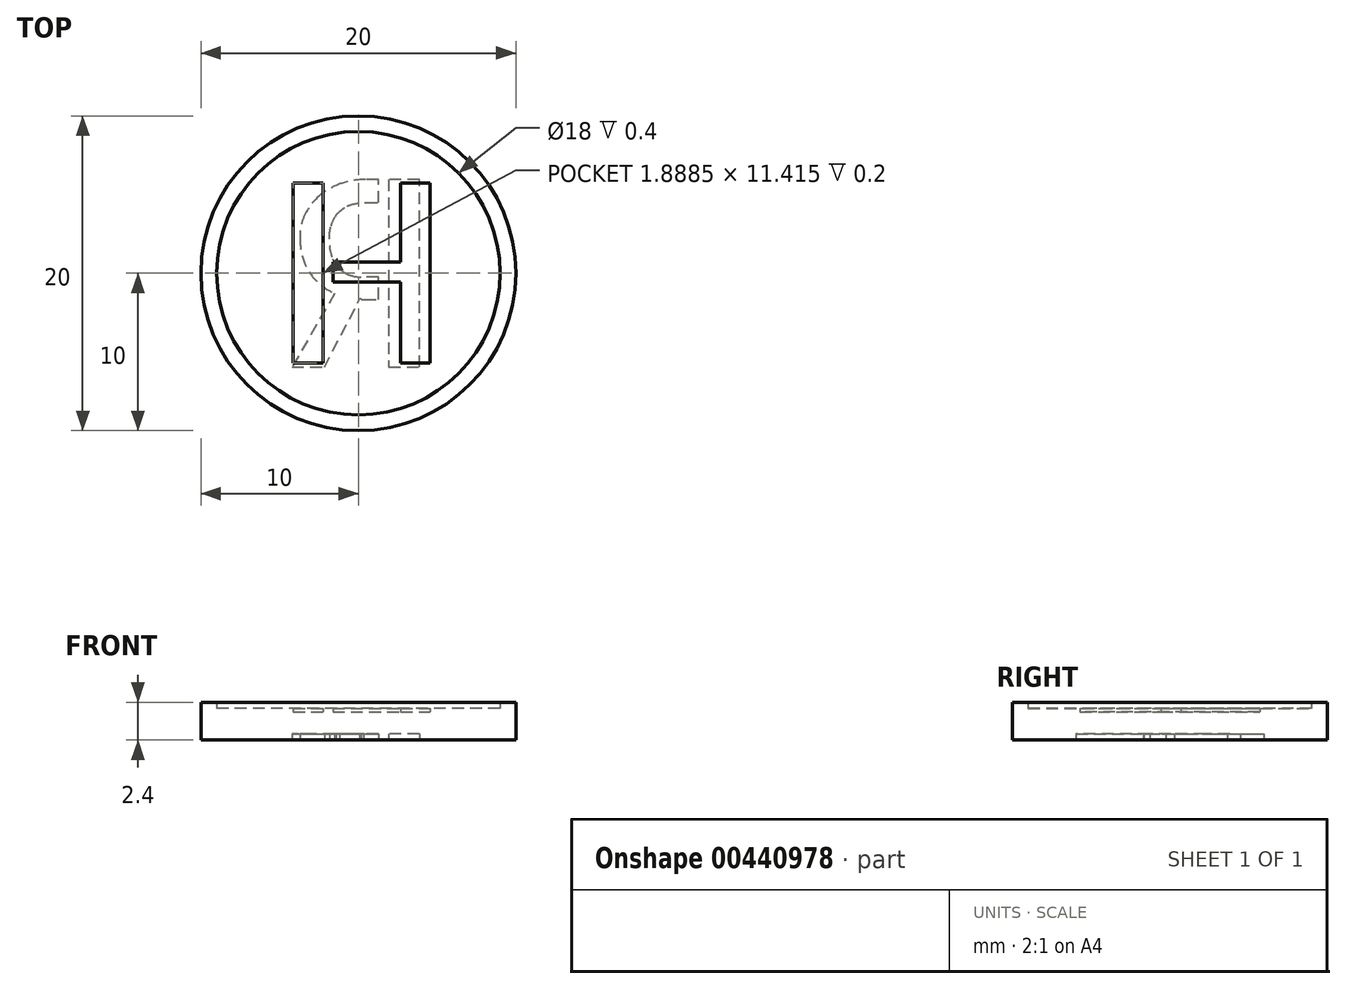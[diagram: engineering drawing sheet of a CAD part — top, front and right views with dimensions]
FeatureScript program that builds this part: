
annotation { "Feature Type Name" : "Feature", "Feature Type Description" : "" }
export const myFeature = defineFeature(function(context is Context, id is Id, definition is map)
    precondition{}
    {
        {
            var Q0;
            Q0=qCreatedBy(makeId("Top.planeOp"),FACE);
            var sketch = newSketch(context, id + "F0", { "sketchPlane" : qUnion([Q0])});
            skCircle(sketch, "E0", {"center": v(0, 0) * mm, "radius": 10 * mm});
            skText(sketch, "E1", { "text": "H", "fontName": "AllertaStencil-Regular.ttf"});
            const initialGuessF0  = {"E1": [-0.0056, -0.0057, 1, 0, 0.01142]};
            skSetInitialGuess(sketch, initialGuessF0);
            skSolve(sketch);
        }
        {
            var Q0;
            Q0=qSketchRegion(id+"F0",true);
            extrude(context, id + "F1", {"entities" : qUnion([Q0]), "depth" : 2 * mm});
        }
        {
            var Q0;
            Q0=makeQuery(id+"F0.imprint","IMPRINT",FACE,{"disambiguationData":[TD([[makeQuery(id+"F0.imprint","IMPRINT",EDGE,{"derivedFrom":sQuery(id+"F0.wireOp",EDGE,"E1.sketch_text.stroke-0")}),-1.0]])]});
            var Q1;
            Q1=makeQuery(id+"F0.imprint","IMPRINT",FACE,{"disambiguationData":[TD([[makeQuery(id+"F0.imprint","IMPRINT",EDGE,{"derivedFrom":sQuery(id+"F0.wireOp",EDGE,"E1.sketch_text.stroke-8")}),-1.0]])]});
            var Q2;
            Q2=makeQuery(id+"F0.imprint","IMPRINT",FACE,{"disambiguationData":[TD([[makeQuery(id+"F0.imprint","IMPRINT",EDGE,{"derivedFrom":sQuery(id+"F0.wireOp",EDGE,"E1.sketch_text.stroke-4")}),-1.0]])]});
            extrude(context, id + "F2", {"entities" : qUnion([Q0, Q1, Q2]), "operationType" : NewBodyOperationType.ADD, "depth" : 1.8 * mm});
        }
        {
            var Q0;
            Q0=makeQuery(id+"F1.opExtrude","CAP_FACE",FACE,{"disambiguationData":[OSD([sQuery(id+"F0.wireOp",EDGE,"E0"),sQuery(id+"F0.wireOp",EDGE,"E1.sketch_text.stroke-0"),sQuery(id+"F0.wireOp",EDGE,"E1.sketch_text.stroke-1"),sQuery(id+"F0.wireOp",EDGE,"E1.sketch_text.stroke-2"),sQuery(id+"F0.wireOp",EDGE,"E1.sketch_text.stroke-3"),sQuery(id+"F0.wireOp",EDGE,"E1.sketch_text.stroke-4"),sQuery(id+"F0.wireOp",EDGE,"E1.sketch_text.stroke-5")])],"isStart":false});
            var sketch = newSketch(context, id + "F3", { "sketchPlane" : qUnion([Q0])});
            skCircle(sketch, "E2.0.0", {"center": v(0, 0) * mm, "radius": 10 * mm});
            skCircle(sketch, "E3.0", {"center": v(0, 0) * mm, "radius": 9 * mm});
            skSolve(sketch);
        }
        {
            var Q0;
            Q0=makeQuery(id+"F3.imprint","IMPRINT",FACE,{"disambiguationData":[TD([[makeQuery(id+"F3.imprint","IMPRINT",EDGE,{"derivedFrom":sQuery(id+"F3.wireOp",EDGE,"E2.0.0")}),1.0]])]});
            extrude(context, id + "F4", {"entities" : qUnion([Q0]), "operationType" : NewBodyOperationType.ADD, "depth" : .4 * mm});
        }
        {
            var Q0;
            {var subQ0=sQuery(id+"F0.wireOp",EDGE,"E1.sketch_text.stroke-5");var subQ1=sQuery(id+"F0.wireOp",EDGE,"E1.sketch_text.stroke-4");var subQ2=sQuery(id+"F0.wireOp",EDGE,"E1.sketch_text.stroke-3");var subQ3=sQuery(id+"F0.wireOp",EDGE,"E1.sketch_text.stroke-2");var subQ4=sQuery(id+"F0.wireOp",EDGE,"E1.sketch_text.stroke-1");var subQ5=sQuery(id+"F0.wireOp",EDGE,"E1.sketch_text.stroke-0");Q0=makeQuery(id+"F2.boolean.opBoolean","MERGE",FACE,{"derivedFrom":[makeQuery(id+"F1.opExtrude","CAP_FACE",FACE,{"disambiguationData":[OSD([sQuery(id+"F0.wireOp",EDGE,"E0"),subQ5,subQ4,subQ3,subQ2,subQ1,subQ0])],"isStart":true}),makeQuery(id+"F2.opExtrude","CAP_FACE",FACE,{"disambiguationData":[OSD([subQ5,subQ4,subQ3,subQ2,subQ1,subQ0])],"isStart":true})]});}
            var sketch = newSketch(context, id + "F5", { "sketchPlane" : qUnion([Q0])});
            skCircle(sketch, "E4.0", {"center": v(0, 0) * mm, "radius": 9 * mm});
            skText(sketch, "E5", { "text": "R", "fontName": "AllertaStencil-Regular.ttf"});
            const initialGuessF5  = {"E5": [0.00533, 0.00597, -1, 0, 0.01193]};
            skSetInitialGuess(sketch, initialGuessF5);
            skSolve(sketch);
        }
        {
            var Q0;
            Q0=makeQuery(id+"F5.imprint","IMPRINT",FACE,{"disambiguationData":[TD([[makeQuery(id+"F5.imprint","IMPRINT",EDGE,{"derivedFrom":sQuery(id+"F5.wireOp",EDGE,"E5.sketch_text.stroke-0")}),-1.0]])]});
            var Q1;
            Q1=makeQuery(id+"F5.imprint","IMPRINT",FACE,{"disambiguationData":[TD([[makeQuery(id+"F5.imprint","IMPRINT",EDGE,{"derivedFrom":sQuery(id+"F5.wireOp",EDGE,"E5.sketch_text.stroke-4")}),-1.0]])]});
            extrude(context, id + "F6", {"entities" : qUnion([Q0, Q1]), "operationType" : NewBodyOperationType.REMOVE, "oppositeDirection" : true, "depth" : .4 * mm});
        }
        {
            var Q0;
            Q0=makeQuery(id+"F2.opExtrude","CAP_FACE",FACE,{"disambiguationData":[OSD([sQuery(id+"F0.wireOp",EDGE,"E1.sketch_text.stroke-0"),sQuery(id+"F0.wireOp",EDGE,"E1.sketch_text.stroke-1"),sQuery(id+"F0.wireOp",EDGE,"E1.sketch_text.stroke-2"),sQuery(id+"F0.wireOp",EDGE,"E1.sketch_text.stroke-3"),sQuery(id+"F0.wireOp",EDGE,"E1.sketch_text.stroke-4"),sQuery(id+"F0.wireOp",EDGE,"E1.sketch_text.stroke-5")])],"isStart":false});
            var Q1;
            Q1=makeQuery(id+"F2.opExtrude","CAP_FACE",FACE,{"disambiguationData":[OSD([sQuery(id+"F0.wireOp",EDGE,"E1.sketch_text.stroke-8"),sQuery(id+"F0.wireOp",EDGE,"E1.sketch_text.stroke-9"),sQuery(id+"F0.wireOp",EDGE,"E1.sketch_text.stroke-10"),sQuery(id+"F0.wireOp",EDGE,"E1.sketch_text.stroke-11")])],"isStart":false});
            var Q2;
            Q2=makeQuery(id+"F2.opExtrude","CAP_FACE",FACE,{"disambiguationData":[OSD([sQuery(id+"F0.wireOp",EDGE,"E1.sketch_text.stroke-4"),sQuery(id+"F0.wireOp",EDGE,"E1.sketch_text.stroke-5"),sQuery(id+"F0.wireOp",EDGE,"E1.sketch_text.stroke-6"),sQuery(id+"F0.wireOp",EDGE,"E1.sketch_text.stroke-7")])],"isStart":false});
            extrude(context, id + "F7", {"entities" : qUnion([Q0, Q1, Q2]), "depth" : .2 * mm});
        }
    });
